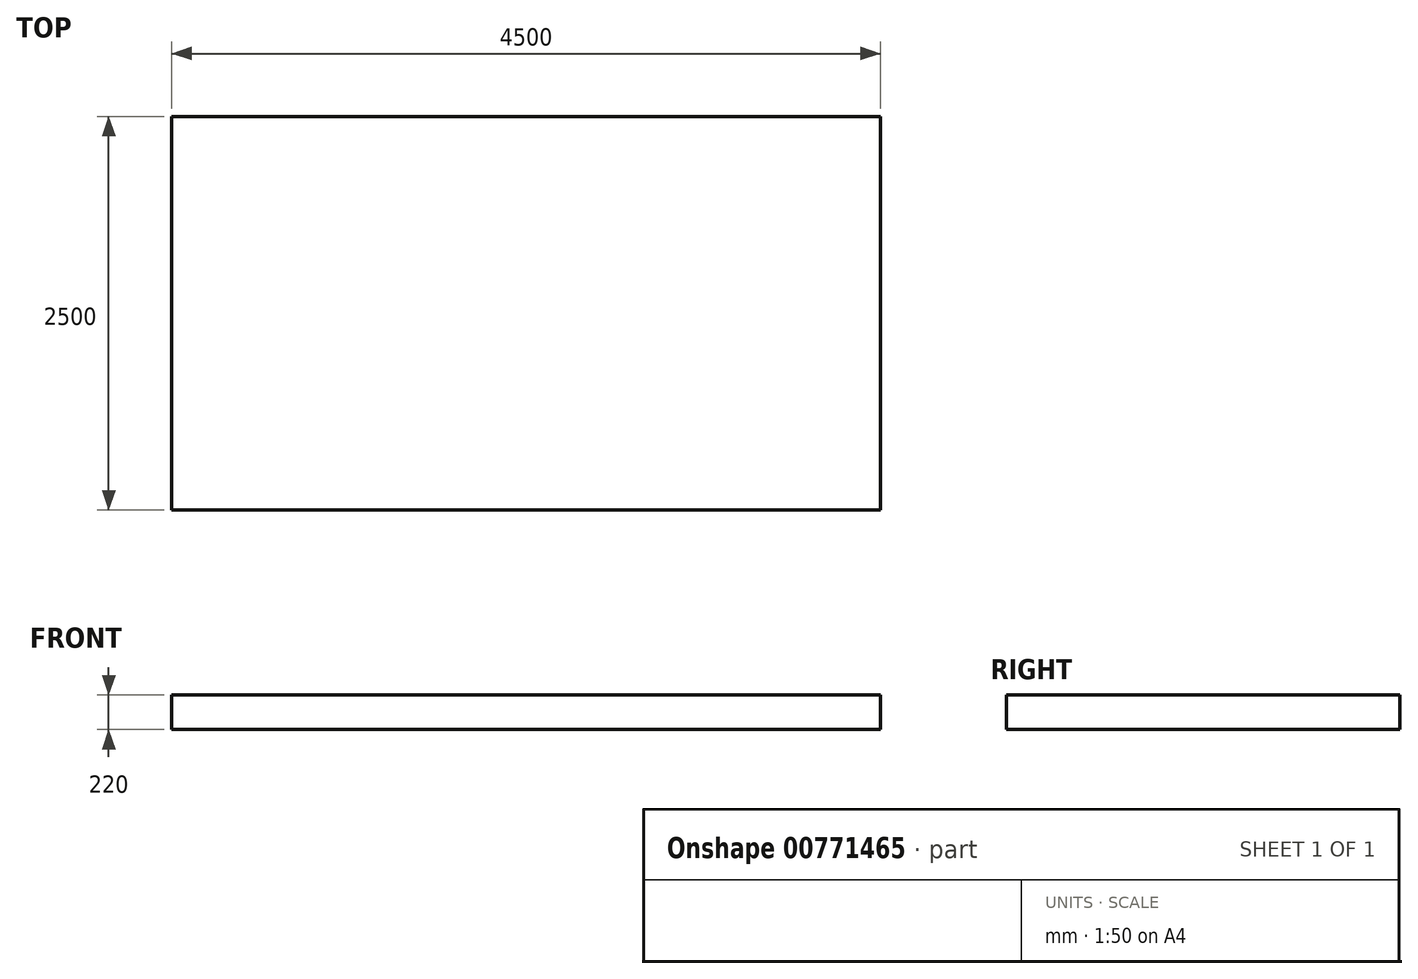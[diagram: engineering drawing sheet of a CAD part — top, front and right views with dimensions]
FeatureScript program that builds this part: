
annotation { "Feature Type Name" : "Feature", "Feature Type Description" : "" }
export const myFeature = defineFeature(function(context is Context, id is Id, definition is map)
    precondition{}
    {
        {
            var Q0;
            Q0=qCreatedBy(makeId("Top.planeOp"),FACE);
            var sketch = newSketch(context, id + "F0", { "sketchPlane" : qUnion([Q0])});
            skLineSegment(sketch, "E0.bottom", {"start": v(2250, -1250) * mm, "end": v(-2250, -1250) * mm});
            skLineSegment(sketch, "E0.top", {"start": v(2250, 1250) * mm, "end": v(-2250, 1250) * mm});
            skLineSegment(sketch, "E0.left", {"start": v(2250, -1250) * mm, "end": v(2250, 1250) * mm});
            skLineSegment(sketch, "E0.right", {"start": v(-2250, -1250) * mm, "end": v(-2250, 1250) * mm});
            skPoint(sketch, "E0.middle", {"position": v(0, 0) * mm});
            skSolve(sketch);
        }
        {
            var Q0;
            Q0 = qSketchRegion(id + "F0", true);
            extrude(context, id + "F1", {"entities" : qUnion([Q0]), "oppositeDirection" : true, "depth" : 220 * mm, "offsetDistance" : 25 * mm});
        }
    });
